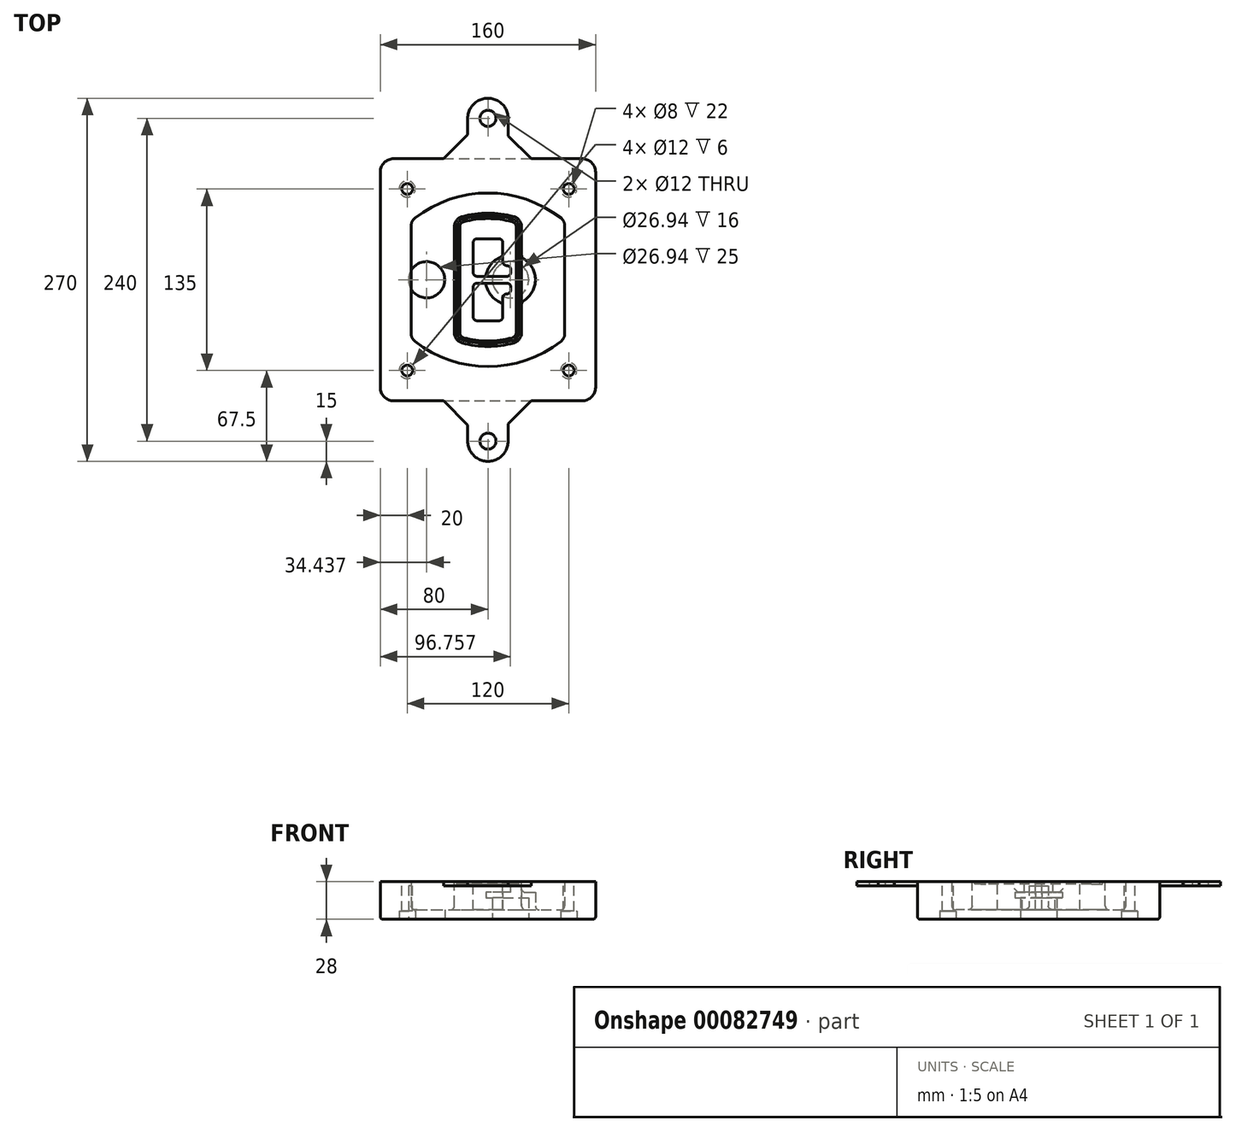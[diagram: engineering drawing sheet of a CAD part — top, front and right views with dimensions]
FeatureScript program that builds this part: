
annotation { "Feature Type Name" : "Feature", "Feature Type Description" : "" }
export const myFeature = defineFeature(function(context is Context, id is Id, definition is map)
    precondition{}
    {
        {
            var Q0;
            Q0=qCreatedBy(makeId("Top.planeOp"),FACE);
            var sketch = newSketch(context, id + "F0", { "sketchPlane" : qUnion([Q0])});
            skPoint(sketch, "E0.rect.middle", {"position": v(0, 0) * mm});
            skLineSegment(sketch, "E1.bottom", {"start": v(-70, -90) * mm, "end": v(70, -90) * mm});
            skLineSegment(sketch, "E1.top", {"start": v(-70, 90) * mm, "end": v(70, 90) * mm});
            skLineSegment(sketch, "E1.left", {"start": v(-80, -80) * mm, "end": v(-80, 80) * mm});
            skLineSegment(sketch, "E1.right", {"start": v(80, -80) * mm, "end": v(80, 80) * mm});
            skLineSegment(sketch, "E2", {"start": v(-80, 90) * mm, "end": v(80, -90) * mm, "construction": true});
            skLineSegment(sketch, "E3", {"start": v(80, 90) * mm, "end": v(-80, -90) * mm, "construction": true});
            skCircle(sketch, "E4", {"center": v(-60, 67.5) * mm, "radius": 4 * mm});
            skCircle(sketch, "E5", {"center": v(60, 67.5) * mm, "radius": 4 * mm});
            skCircle(sketch, "E6", {"center": v(60, -67.5) * mm, "radius": 4 * mm});
            skCircle(sketch, "E7", {"center": v(-60, -67.5) * mm, "radius": 4 * mm});
            skLineSegment(sketch, "E8", {"start": v(-60, 67.5) * mm, "end": v(60, 67.5) * mm, "construction": true});
            skLineSegment(sketch, "E9", {"start": v(60, 67.5) * mm, "end": v(60, -67.5) * mm, "construction": true});
            skLineSegment(sketch, "E10", {"start": v(60, -67.5) * mm, "end": v(-60, -67.5) * mm, "construction": true});
            skLineSegment(sketch, "E11", {"start": v(-60, -67.5) * mm, "end": v(-60, 67.5) * mm, "construction": true});
            skLineSegment(sketch, "E12", {"start": v(-60, 40.3) * mm, "end": v(-60, -40.3) * mm});
            skLineSegment(sketch, "E13", {"start": v(60, 40.3) * mm, "end": v(60, -40.3) * mm});
            skArc(sketch, "E14", {"start": v(56.15, 48.18) * mm, "mid": v(0, 67.5) * mm, "end": v(-56.15, 48.18) * mm});
            skArc(sketch, "E15", {"start": v(-56.15, -48.18) * mm, "mid": v(0, -67.5) * mm, "end": v(56.15, -48.18) * mm});
            skLineSegment(sketch, "E16", {"start": v(-60, 0) * mm, "end": v(60, 0) * mm, "construction": true});
            skPoint(sketch, "E17.visualSharp", {"position": v(-60, -45) * mm});
            skArc(sketch, "E17.filletArc", {"start": v(-60, -40.3) * mm, "mid": v(-58.99, -44.68) * mm, "end": v(-56.15, -48.18) * mm});
            skPoint(sketch, "E18.visualSharp", {"position": v(-60, 45) * mm});
            skArc(sketch, "E18.filletArc", {"start": v(-56.15, 48.18) * mm, "mid": v(-58.99, 44.68) * mm, "end": v(-60, 40.3) * mm});
            skPoint(sketch, "E19.visualSharp", {"position": v(60, 45) * mm});
            skArc(sketch, "E19.filletArc", {"start": v(60, 40.3) * mm, "mid": v(58.99, 44.68) * mm, "end": v(56.15, 48.18) * mm});
            skPoint(sketch, "E20.visualSharp", {"position": v(60, -45) * mm});
            skArc(sketch, "E20.filletArc", {"start": v(56.15, -48.18) * mm, "mid": v(58.99, -44.68) * mm, "end": v(60, -40.3) * mm});
            skPoint(sketch, "E21.visualSharp", {"position": v(-80, 90) * mm});
            skArc(sketch, "E21.filletArc", {"start": v(-70, 90) * mm, "mid": v(-77.07, 87.07) * mm, "end": v(-80, 80) * mm});
            skPoint(sketch, "E22.visualSharp", {"position": v(80, 90) * mm});
            skArc(sketch, "E22.filletArc", {"start": v(80, 80) * mm, "mid": v(77.07, 87.07) * mm, "end": v(70, 90) * mm});
            skPoint(sketch, "E23.visualSharp", {"position": v(80, -90) * mm});
            skArc(sketch, "E23.filletArc", {"start": v(70, -90) * mm, "mid": v(77.07, -87.07) * mm, "end": v(80, -80) * mm});
            skPoint(sketch, "E24.visualSharp", {"position": v(-80, -90) * mm});
            skArc(sketch, "E24.filletArc", {"start": v(-80, -80) * mm, "mid": v(-77.07, -87.07) * mm, "end": v(-70, -90) * mm});
            skArc(sketch, "E25.0", {"start": v(57, 40.3) * mm, "mid": v(56.3, 43.36) * mm, "end": v(54.3, 45.81) * mm});
            skLineSegment(sketch, "E25.1", {"start": v(57, 40.3) * mm, "end": v(57, -40.3) * mm});
            skArc(sketch, "E25.2", {"start": v(54.3, -45.81) * mm, "mid": v(56.3, -43.36) * mm, "end": v(57, -40.3) * mm});
            skArc(sketch, "E25.3", {"start": v(-54.3, -45.81) * mm, "mid": v(0, -64.5) * mm, "end": v(54.3, -45.81) * mm});
            skArc(sketch, "E25.4", {"start": v(-57, -40.3) * mm, "mid": v(-56.3, -43.36) * mm, "end": v(-54.3, -45.81) * mm});
            skArc(sketch, "E25.5", {"start": v(54.3, 45.81) * mm, "mid": v(0, 64.5) * mm, "end": v(-54.3, 45.81) * mm});
            skLineSegment(sketch, "E25.6", {"start": v(-57, 40.3) * mm, "end": v(-57, -40.3) * mm});
            skArc(sketch, "E25.7", {"start": v(-54.3, 45.81) * mm, "mid": v(-56.3, 43.36) * mm, "end": v(-57, 40.3) * mm});
            skArc(sketch, "E26.0", {"start": v(-58.62, 51.33) * mm, "mid": v(-62.58, 46.43) * mm, "end": v(-64, 40.3) * mm});
            skArc(sketch, "E26.1", {"start": v(58.62, 51.33) * mm, "mid": v(0, 71.5) * mm, "end": v(-58.62, 51.33) * mm});
            skArc(sketch, "E26.2", {"start": v(64, 40.3) * mm, "mid": v(62.58, 46.43) * mm, "end": v(58.62, 51.33) * mm});
            skLineSegment(sketch, "E26.3", {"start": v(64, 40.3) * mm, "end": v(64, -40.3) * mm});
            skArc(sketch, "E26.4", {"start": v(58.62, -51.33) * mm, "mid": v(62.58, -46.43) * mm, "end": v(64, -40.3) * mm});
            skLineSegment(sketch, "E26.5", {"start": v(-64, 40.3) * mm, "end": v(-64, -40.3) * mm});
            skArc(sketch, "E26.6", {"start": v(-58.62, -51.33) * mm, "mid": v(0, -71.5) * mm, "end": v(58.62, -51.33) * mm});
            skArc(sketch, "E26.7", {"start": v(-64, -40.3) * mm, "mid": v(-62.58, -46.43) * mm, "end": v(-58.62, -51.33) * mm});
            skSolve(sketch);
        }
        {
            var Q0;
            Q0=makeQuery(id+"F0.imprint","IMPRINT",FACE,{"disambiguationData":[TD([[makeQuery(id+"F0.imprint","IMPRINT",EDGE,{"derivedFrom":sQuery(id+"F0.wireOp",EDGE,"E1.bottom")}),1.0]])]});
            var Q1;
            Q1=makeQuery(id+"F0.imprint","IMPRINT",FACE,{"disambiguationData":[TD([[makeQuery(id+"F0.imprint","IMPRINT",EDGE,{"derivedFrom":sQuery(id+"F0.wireOp",EDGE,"E12")}),1.0]])]});
            var Q2;
            Q2=makeQuery(id+"F0.imprint","IMPRINT",FACE,{"disambiguationData":[TD([[makeQuery(id+"F0.imprint","IMPRINT",EDGE,{"derivedFrom":sQuery(id+"F0.wireOp",EDGE,"E25.0")}),1.0]])]});
            var Q3;
            Q3=makeQuery(id+"F0.imprint","IMPRINT",FACE,{"disambiguationData":[TD([[makeQuery(id+"F0.imprint","IMPRINT",EDGE,{"derivedFrom":sQuery(id+"F0.wireOp",EDGE,"E12")}),-1.0]])]});
            extrude(context, id + "F1", {"entities" : qUnion([Q0, Q1, Q2, Q3]), "oppositeDirection" : true, "depth" : 25 * mm});
        }
        {
            var Q0;
            Q0=makeQuery(id+"F0.imprint","IMPRINT",FACE,{"disambiguationData":[TD([[makeQuery(id+"F0.imprint","IMPRINT",EDGE,{"derivedFrom":sQuery(id+"F0.wireOp",EDGE,"E12")}),1.0]])]});
            extrude(context, id + "F2", {"entities" : qUnion([Q0]), "operationType" : NewBodyOperationType.ADD, "depth" : 3 * mm});
        }
        {
            var Q0;
            Q0=makeQuery(id+"F0.imprint","IMPRINT",FACE,{"disambiguationData":[TD([[makeQuery(id+"F0.imprint","IMPRINT",EDGE,{"derivedFrom":sQuery(id+"F0.wireOp",EDGE,"E25.0")}),1.0]])]});
            extrude(context, id + "F3", {"entities" : qUnion([Q0]), "operationType" : NewBodyOperationType.REMOVE, "oppositeDirection" : true, "depth" : 18 * mm});
        }
        {
            var Q0;
            Q0=makeQuery(id+"F2.opExtrude","CAP_FACE",FACE,{"disambiguationData":[OSD([sQuery(id+"F0.wireOp",EDGE,"E12"),sQuery(id+"F0.wireOp",EDGE,"E13"),sQuery(id+"F0.wireOp",EDGE,"E14"),sQuery(id+"F0.wireOp",EDGE,"E15"),sQuery(id+"F0.wireOp",EDGE,"E17.filletArc"),sQuery(id+"F0.wireOp",EDGE,"E18.filletArc"),sQuery(id+"F0.wireOp",EDGE,"E19.filletArc"),sQuery(id+"F0.wireOp",EDGE,"E20.filletArc"),sQuery(id+"F0.wireOp",EDGE,"E25.0"),sQuery(id+"F0.wireOp",EDGE,"E25.1"),sQuery(id+"F0.wireOp",EDGE,"E25.2"),sQuery(id+"F0.wireOp",EDGE,"E25.3"),sQuery(id+"F0.wireOp",EDGE,"E25.4"),sQuery(id+"F0.wireOp",EDGE,"E25.5"),sQuery(id+"F0.wireOp",EDGE,"E25.6"),sQuery(id+"F0.wireOp",EDGE,"E25.7")])],"isStart":false});
            var sketch = newSketch(context, id + "F4", { "sketchPlane" : qUnion([Q0])});
            skArc(sketch, "E27.0", {"start": v(-19.08, -46.97) * mm, "mid": v(0, -49.5) * mm, "end": v(19.08, -46.97) * mm});
            skArc(sketch, "E28.0", {"start": v(19.08, 46.97) * mm, "mid": v(0, 49.5) * mm, "end": v(-19.08, 46.97) * mm});
            skLineSegment(sketch, "E29", {"start": v(-25, 39.25) * mm, "end": v(-25, -39.25) * mm});
            skLineSegment(sketch, "E30", {"start": v(25, 39.25) * mm, "end": v(25, -39.25) * mm});
            skLineSegment(sketch, "E31", {"start": v(-25, 45.1) * mm, "end": v(25, 45.1) * mm, "construction": true});
            skLineSegment(sketch, "E32", {"start": v(-25, -45.1) * mm, "end": v(25, -45.1) * mm, "construction": true});
            skPoint(sketch, "E33.visualSharp", {"position": v(-25, 45.1) * mm});
            skArc(sketch, "E33.filletArc", {"start": v(-19.08, 46.97) * mm, "mid": v(-23.35, 44.11) * mm, "end": v(-25, 39.25) * mm});
            skPoint(sketch, "E34.visualSharp", {"position": v(25, 45.1) * mm});
            skArc(sketch, "E34.filletArc", {"start": v(25, 39.25) * mm, "mid": v(23.35, 44.11) * mm, "end": v(19.08, 46.97) * mm});
            skPoint(sketch, "E35.visualSharp", {"position": v(25, -45.1) * mm});
            skArc(sketch, "E35.filletArc", {"start": v(19.08, -46.97) * mm, "mid": v(23.35, -44.11) * mm, "end": v(25, -39.25) * mm});
            skPoint(sketch, "E36.visualSharp", {"position": v(-25, -45.1) * mm});
            skArc(sketch, "E36.filletArc", {"start": v(-25, -39.25) * mm, "mid": v(-23.35, -44.11) * mm, "end": v(-19.08, -46.97) * mm});
            skArc(sketch, "E37.0", {"start": v(54.3, 45.81) * mm, "mid": v(0, 64.5) * mm, "end": v(-54.3, 45.81) * mm});
            skArc(sketch, "E37.1", {"start": v(-54.3, 45.81) * mm, "mid": v(-56.3, 43.36) * mm, "end": v(-57, 40.3) * mm});
            skLineSegment(sketch, "E37.2", {"start": v(-57, 40.3) * mm, "end": v(-57, -40.3) * mm});
            skArc(sketch, "E37.3", {"start": v(-57, -40.3) * mm, "mid": v(-56.3, -43.36) * mm, "end": v(-54.3, -45.81) * mm});
            skArc(sketch, "E37.4", {"start": v(-54.3, -45.81) * mm, "mid": v(0, -64.5) * mm, "end": v(54.3, -45.81) * mm});
            skArc(sketch, "E37.5", {"start": v(54.3, -45.81) * mm, "mid": v(56.3, -43.36) * mm, "end": v(57, -40.3) * mm});
            skLineSegment(sketch, "E37.6", {"start": v(57, 40.3) * mm, "end": v(57, -40.3) * mm});
            skArc(sketch, "E37.7", {"start": v(57, 40.3) * mm, "mid": v(56.3, 43.36) * mm, "end": v(54.3, 45.81) * mm});
            skLineSegment(sketch, "E38.0", {"start": v(23, 39.25) * mm, "end": v(23, -39.25) * mm});
            skArc(sketch, "E38.1", {"start": v(18.56, -45.04) * mm, "mid": v(21.76, -42.9) * mm, "end": v(23, -39.25) * mm});
            skArc(sketch, "E38.2", {"start": v(-18.56, -45.04) * mm, "mid": v(0, -47.5) * mm, "end": v(18.56, -45.04) * mm});
            skArc(sketch, "E38.3", {"start": v(-23, -39.25) * mm, "mid": v(-21.76, -42.9) * mm, "end": v(-18.56, -45.04) * mm});
            skLineSegment(sketch, "E38.4", {"start": v(-23, 39.25) * mm, "end": v(-23, -39.25) * mm});
            skArc(sketch, "E38.5", {"start": v(23, 39.25) * mm, "mid": v(21.76, 42.9) * mm, "end": v(18.56, 45.04) * mm});
            skArc(sketch, "E38.6", {"start": v(-18.56, 45.04) * mm, "mid": v(-21.76, 42.9) * mm, "end": v(-23, 39.25) * mm});
            skArc(sketch, "E38.7", {"start": v(18.56, 45.04) * mm, "mid": v(0, 47.5) * mm, "end": v(-18.56, 45.04) * mm});
            skArc(sketch, "E39.0", {"start": v(21, 39.25) * mm, "mid": v(20.18, 41.68) * mm, "end": v(18.04, 43.1) * mm});
            skLineSegment(sketch, "E39.1", {"start": v(21, 39.25) * mm, "end": v(21, -39.25) * mm});
            skArc(sketch, "E39.2", {"start": v(18.04, -43.1) * mm, "mid": v(20.18, -41.68) * mm, "end": v(21, -39.25) * mm});
            skArc(sketch, "E39.3", {"start": v(-18.04, -43.1) * mm, "mid": v(0, -45.5) * mm, "end": v(18.04, -43.1) * mm});
            skArc(sketch, "E39.4", {"start": v(-21, -39.25) * mm, "mid": v(-20.18, -41.68) * mm, "end": v(-18.04, -43.1) * mm});
            skArc(sketch, "E39.5", {"start": v(18.04, 43.1) * mm, "mid": v(0, 45.5) * mm, "end": v(-18.04, 43.1) * mm});
            skLineSegment(sketch, "E39.6", {"start": v(-21, 39.25) * mm, "end": v(-21, -39.25) * mm});
            skArc(sketch, "E39.7", {"start": v(-18.04, 43.1) * mm, "mid": v(-20.18, 41.68) * mm, "end": v(-21, 39.25) * mm});
            skLineSegment(sketch, "E40", {"start": v(-25, 0) * mm, "end": v(25, 0) * mm, "construction": true});
            skLineSegment(sketch, "E41", {"start": v(-11, 5.5) * mm, "end": v(-11, 27.5) * mm});
            skLineSegment(sketch, "E42", {"start": v(-8, 30.5) * mm, "end": v(8, 30.5) * mm});
            skLineSegment(sketch, "E43", {"start": v(11, 27.5) * mm, "end": v(11, 13.5) * mm});
            skLineSegment(sketch, "E44", {"start": v(14, 10.5) * mm, "end": v(14, 10.5) * mm});
            skLineSegment(sketch, "E45", {"start": v(17, 7.5) * mm, "end": v(17, 5.5) * mm});
            skLineSegment(sketch, "E46", {"start": v(14, 2.5) * mm, "end": v(-8, 2.5) * mm});
            skPoint(sketch, "E47.visualSharp", {"position": v(-11, 30.5) * mm});
            skArc(sketch, "E47.filletArc", {"start": v(-8, 30.5) * mm, "mid": v(-10.12, 29.62) * mm, "end": v(-11, 27.5) * mm});
            skPoint(sketch, "E48.visualSharp", {"position": v(11, 30.5) * mm});
            skArc(sketch, "E48.filletArc", {"start": v(11, 27.5) * mm, "mid": v(10.12, 29.62) * mm, "end": v(8, 30.5) * mm});
            skPoint(sketch, "E49.visualSharp", {"position": v(11, 10.5) * mm});
            skArc(sketch, "E49.filletArc", {"start": v(11, 13.5) * mm, "mid": v(11.88, 11.38) * mm, "end": v(14, 10.5) * mm});
            skPoint(sketch, "E50.visualSharp", {"position": v(17, 10.5) * mm});
            skArc(sketch, "E50.filletArc", {"start": v(17, 7.5) * mm, "mid": v(16.12, 9.62) * mm, "end": v(14, 10.5) * mm});
            skPoint(sketch, "E51.visualSharp", {"position": v(17, 2.5) * mm});
            skArc(sketch, "E51.filletArc", {"start": v(14, 2.5) * mm, "mid": v(16.12, 3.38) * mm, "end": v(17, 5.5) * mm});
            skPoint(sketch, "E52.visualSharp", {"position": v(-11, 2.5) * mm});
            skArc(sketch, "E52.filletArc", {"start": v(-11, 5.5) * mm, "mid": v(-10.12, 3.38) * mm, "end": v(-8, 2.5) * mm});
            skLineSegment(sketch, "E53.0.MirrorCS", {"start": v(14, -2.5) * mm, "end": v(-8, -2.5) * mm});
            skArc(sketch, "E54.0.MirrorCS", {"start": v(-11, -5.5) * mm, "mid": v(-10.12, -3.38) * mm, "end": v(-8, -2.5) * mm});
            skLineSegment(sketch, "E55.0.MirrorCS", {"start": v(-11, -5.5) * mm, "end": v(-11, -27.5) * mm});
            skArc(sketch, "E56.0.MirrorCS", {"start": v(-8, -30.5) * mm, "mid": v(-10.12, -29.62) * mm, "end": v(-11, -27.5) * mm});
            skLineSegment(sketch, "E57.0.MirrorCS", {"start": v(-8, -30.5) * mm, "end": v(8, -30.5) * mm});
            skArc(sketch, "E58.0.MirrorCS", {"start": v(11, -27.5) * mm, "mid": v(10.12, -29.62) * mm, "end": v(8, -30.5) * mm});
            skLineSegment(sketch, "E59.0.MirrorCS", {"start": v(11, -27.5) * mm, "end": v(11, -13.5) * mm});
            skArc(sketch, "E60.0.MirrorCS", {"start": v(11, -13.5) * mm, "mid": v(11.88, -11.38) * mm, "end": v(14, -10.5) * mm});
            skArc(sketch, "E61.0.MirrorCS", {"start": v(17, -7.5) * mm, "mid": v(16.12, -9.62) * mm, "end": v(14, -10.5) * mm});
            skLineSegment(sketch, "E62.0.MirrorCS", {"start": v(17, -7.5) * mm, "end": v(17, -5.5) * mm});
            skArc(sketch, "E63.0.MirrorCS", {"start": v(14, -2.5) * mm, "mid": v(16.12, -3.38) * mm, "end": v(17, -5.5) * mm});
            skSolve(sketch);
        }
        {
            var Q0;
            Q0=makeQuery(id+"F4.imprint","IMPRINT",FACE,{"disambiguationData":[TD([[makeQuery(id+"F4.imprint","IMPRINT",EDGE,{"derivedFrom":sQuery(id+"F4.wireOp",EDGE,"E27.0")}),1.0]])]});
            var Q1;
            Q1=makeQuery(id+"F4.imprint","IMPRINT",FACE,{"disambiguationData":[TD([[makeQuery(id+"F4.imprint","IMPRINT",EDGE,{"derivedFrom":sQuery(id+"F4.wireOp",EDGE,"E38.0")}),-1.0]])]});
            var Q2;
            Q2=makeQuery(id+"F4.imprint","IMPRINT",FACE,{"disambiguationData":[TD([[makeQuery(id+"F4.imprint","IMPRINT",EDGE,{"derivedFrom":sQuery(id+"F4.wireOp",EDGE,"E39.0")}),1.0]])]});
            extrude(context, id + "F5", {"entities" : qUnion([Q0, Q1, Q2]), "operationType" : NewBodyOperationType.ADD, "endBound" : BoundingType.UP_TO_NEXT, "oppositeDirection" : true, "depth" : 25 * mm});
        }
        {
            var Q0;
            Q0=makeQuery(id+"F4.imprint","IMPRINT",FACE,{"disambiguationData":[TD([[makeQuery(id+"F4.imprint","IMPRINT",EDGE,{"derivedFrom":sQuery(id+"F4.wireOp",EDGE,"E38.0")}),-1.0]])]});
            extrude(context, id + "F6", {"entities" : qUnion([Q0]), "operationType" : NewBodyOperationType.REMOVE, "oppositeDirection" : true, "depth" : 2 * mm});
        }
        {
            var Q0;
            Q0=makeQuery(id+"F1.opExtrude","CAP_FACE",FACE,{"disambiguationData":[OSD([sQuery(id+"F0.wireOp",EDGE,"E1.bottom"),sQuery(id+"F0.wireOp",EDGE,"E1.top"),sQuery(id+"F0.wireOp",EDGE,"E1.left"),sQuery(id+"F0.wireOp",EDGE,"E1.right"),sQuery(id+"F0.wireOp",EDGE,"E4"),sQuery(id+"F0.wireOp",EDGE,"E5"),sQuery(id+"F0.wireOp",EDGE,"E6"),sQuery(id+"F0.wireOp",EDGE,"E7"),sQuery(id+"F0.wireOp",EDGE,"E21.filletArc"),sQuery(id+"F0.wireOp",EDGE,"E22.filletArc"),sQuery(id+"F0.wireOp",EDGE,"E23.filletArc"),sQuery(id+"F0.wireOp",EDGE,"E24.filletArc")])],"isStart":false});
            var sketch = newSketch(context, id + "F7", { "sketchPlane" : qUnion([Q0])});
            skCircle(sketch, "E64", {"center": v(16.76, 0) * mm, "radius": 13.47 * mm});
            skCircle(sketch, "E65", {"center": v(-45.56, 0) * mm, "radius": 13.47 * mm});
            skLineSegment(sketch, "E66", {"start": v(80, 0) * mm, "end": v(-80, 0) * mm});
            skCircle(sketch, "E67", {"center": v(16.76, 0) * mm, "radius": 18.47 * mm});
            skCircle(sketch, "E68", {"center": v(60, -67.5) * mm, "radius": 6 * mm});
            skCircle(sketch, "E69", {"center": v(-60, -67.5) * mm, "radius": 6 * mm});
            skCircle(sketch, "E70", {"center": v(-60, 67.5) * mm, "radius": 6 * mm});
            skCircle(sketch, "E71", {"center": v(60, 67.5) * mm, "radius": 6 * mm});
            skSolve(sketch);
        }
        {
            var Q0;
            {var subQ1=sQuery(id+"F7.wireOp",EDGE,"E66");var subQ4=sQuery(id+"F7.wireOp",EDGE,"E64");var subQ6=makeQuery(id+"F7.imprint","INTERSECT",VERTEX,{"disambiguationData":[OD(0.0)],"derivedFrom":[subQ4,subQ1]});Q0=makeQuery(id+"F7.imprint","IMPRINT",FACE,{"disambiguationData":[TD([[makeQuery(id+"F7.imprint","IMPRINT",EDGE,{"disambiguationData":[TD([[subQ6,-1.0]])],"derivedFrom":subQ4}),-1.0]])]});}
            var Q1;
            {var subQ0=sQuery(id+"F7.wireOp",EDGE,"E66");var subQ1=sQuery(id+"F7.wireOp",EDGE,"E64");var subQ3=makeQuery(id+"F7.imprint","INTERSECT",VERTEX,{"disambiguationData":[OD(0.0)],"derivedFrom":[subQ1,subQ0]});Q1=makeQuery(id+"F7.imprint","IMPRINT",FACE,{"disambiguationData":[TD([[makeQuery(id+"F7.imprint","IMPRINT",EDGE,{"disambiguationData":[TD([[subQ3,-1.0]])],"derivedFrom":subQ1}),1.0]])]});}
            var Q2;
            {var subQ0=sQuery(id+"F7.wireOp",EDGE,"E66");var subQ1=sQuery(id+"F7.wireOp",EDGE,"E64");var subQ3=makeQuery(id+"F7.imprint","INTERSECT",VERTEX,{"disambiguationData":[OD(0.0)],"derivedFrom":[subQ1,subQ0]});Q2=makeQuery(id+"F7.imprint","IMPRINT",FACE,{"disambiguationData":[TD([[makeQuery(id+"F7.imprint","IMPRINT",EDGE,{"disambiguationData":[TD([[subQ3,1.0]])],"derivedFrom":subQ1}),1.0]])]});}
            var Q3;
            {var subQ1=sQuery(id+"F7.wireOp",EDGE,"E66");var subQ4=sQuery(id+"F7.wireOp",EDGE,"E64");var subQ6=makeQuery(id+"F7.imprint","INTERSECT",VERTEX,{"disambiguationData":[OD(0.0)],"derivedFrom":[subQ4,subQ1]});Q3=makeQuery(id+"F7.imprint","IMPRINT",FACE,{"disambiguationData":[TD([[makeQuery(id+"F7.imprint","IMPRINT",EDGE,{"disambiguationData":[TD([[subQ6,1.0]])],"derivedFrom":subQ4}),-1.0]])]});}
            extrude(context, id + "F8", {"entities" : qUnion([Q0, Q1, Q2, Q3]), "operationType" : NewBodyOperationType.ADD, "oppositeDirection" : true, "depth" : 20 * mm});
        }
        {
            var Q0;
            {var subQ0=sQuery(id+"F7.wireOp",EDGE,"E66");var subQ1=sQuery(id+"F7.wireOp",EDGE,"E64");var subQ3=makeQuery(id+"F7.imprint","INTERSECT",VERTEX,{"disambiguationData":[OD(0.0)],"derivedFrom":[subQ1,subQ0]});Q0=makeQuery(id+"F7.imprint","IMPRINT",FACE,{"disambiguationData":[TD([[makeQuery(id+"F7.imprint","IMPRINT",EDGE,{"disambiguationData":[TD([[subQ3,-1.0]])],"derivedFrom":subQ1}),1.0]])]});}
            var Q1;
            {var subQ0=sQuery(id+"F7.wireOp",EDGE,"E66");var subQ1=sQuery(id+"F7.wireOp",EDGE,"E64");var subQ3=makeQuery(id+"F7.imprint","INTERSECT",VERTEX,{"disambiguationData":[OD(0.0)],"derivedFrom":[subQ1,subQ0]});Q1=makeQuery(id+"F7.imprint","IMPRINT",FACE,{"disambiguationData":[TD([[makeQuery(id+"F7.imprint","IMPRINT",EDGE,{"disambiguationData":[TD([[subQ3,1.0]])],"derivedFrom":subQ1}),1.0]])]});}
            extrude(context, id + "F9", {"entities" : qUnion([Q0, Q1]), "operationType" : NewBodyOperationType.REMOVE, "oppositeDirection" : true, "depth" : 16 * mm});
        }
        {
            var Q0;
            {var subQ0=sQuery(id+"F7.wireOp",EDGE,"E66");var subQ1=sQuery(id+"F7.wireOp",EDGE,"E65");var subQ3=makeQuery(id+"F7.imprint","INTERSECT",VERTEX,{"disambiguationData":[OD(0.0)],"derivedFrom":[subQ1,subQ0]});Q0=makeQuery(id+"F7.imprint","IMPRINT",FACE,{"disambiguationData":[TD([[makeQuery(id+"F7.imprint","IMPRINT",EDGE,{"disambiguationData":[TD([[subQ3,-1.0]])],"derivedFrom":subQ1}),1.0]])]});}
            var Q1;
            {var subQ0=sQuery(id+"F7.wireOp",EDGE,"E66");var subQ1=sQuery(id+"F7.wireOp",EDGE,"E65");var subQ3=makeQuery(id+"F7.imprint","INTERSECT",VERTEX,{"disambiguationData":[OD(0.0)],"derivedFrom":[subQ1,subQ0]});Q1=makeQuery(id+"F7.imprint","IMPRINT",FACE,{"disambiguationData":[TD([[makeQuery(id+"F7.imprint","IMPRINT",EDGE,{"disambiguationData":[TD([[subQ3,1.0]])],"derivedFrom":subQ1}),1.0]])]});}
            extrude(context, id + "F10", {"entities" : qUnion([Q0, Q1]), "operationType" : NewBodyOperationType.REMOVE, "oppositeDirection" : true, "depth" : 25 * mm});
        }
        {
            var Q0;
            Q0=makeQuery(id+"F7.imprint","IMPRINT",FACE,{"disambiguationData":[TD([[makeQuery(id+"F7.imprint","IMPRINT",EDGE,{"derivedFrom":sQuery(id+"F7.wireOp",EDGE,"E68")}),1.0]])]});
            var Q1;
            Q1=makeQuery(id+"F7.imprint","IMPRINT",FACE,{"disambiguationData":[TD([[makeQuery(id+"F7.imprint","IMPRINT",EDGE,{"derivedFrom":makeQuery(id+"F1.opExtrude","CAP_EDGE",EDGE,{"disambiguationData":[OSD([sQuery(id+"F0.wireOp",EDGE,"E5")])],"isStart":false})}),-1.0]])]});
            var Q2;
            Q2=makeQuery(id+"F7.imprint","IMPRINT",FACE,{"disambiguationData":[TD([[makeQuery(id+"F7.imprint","IMPRINT",EDGE,{"derivedFrom":sQuery(id+"F7.wireOp",EDGE,"E69")}),1.0]])]});
            var Q3;
            Q3=makeQuery(id+"F7.imprint","IMPRINT",FACE,{"disambiguationData":[TD([[makeQuery(id+"F7.imprint","IMPRINT",EDGE,{"derivedFrom":makeQuery(id+"F1.opExtrude","CAP_EDGE",EDGE,{"disambiguationData":[OSD([sQuery(id+"F0.wireOp",EDGE,"E4")])],"isStart":false})}),-1.0]])]});
            var Q4;
            Q4=makeQuery(id+"F7.imprint","IMPRINT",FACE,{"disambiguationData":[TD([[makeQuery(id+"F7.imprint","IMPRINT",EDGE,{"derivedFrom":sQuery(id+"F7.wireOp",EDGE,"E70")}),1.0]])]});
            var Q5;
            Q5=makeQuery(id+"F7.imprint","IMPRINT",FACE,{"disambiguationData":[TD([[makeQuery(id+"F7.imprint","IMPRINT",EDGE,{"derivedFrom":makeQuery(id+"F1.opExtrude","CAP_EDGE",EDGE,{"disambiguationData":[OSD([sQuery(id+"F0.wireOp",EDGE,"E7")])],"isStart":false})}),-1.0]])]});
            var Q6;
            Q6=makeQuery(id+"F7.imprint","IMPRINT",FACE,{"disambiguationData":[TD([[makeQuery(id+"F7.imprint","IMPRINT",EDGE,{"derivedFrom":sQuery(id+"F7.wireOp",EDGE,"E71")}),1.0]])]});
            var Q7;
            Q7=makeQuery(id+"F7.imprint","IMPRINT",FACE,{"disambiguationData":[TD([[makeQuery(id+"F7.imprint","IMPRINT",EDGE,{"derivedFrom":makeQuery(id+"F1.opExtrude","CAP_EDGE",EDGE,{"disambiguationData":[OSD([sQuery(id+"F0.wireOp",EDGE,"E6")])],"isStart":false})}),-1.0]])]});
            extrude(context, id + "F11", {"entities" : qUnion([Q0, Q1, Q2, Q3, Q4, Q5, Q6, Q7]), "operationType" : NewBodyOperationType.REMOVE, "oppositeDirection" : true, "depth" : 6 * mm});
        }
        {
            var Q0;
            Q0=makeQuery(id+"F9.boolean.opBoolean","COPY",FACE,{"derivedFrom":makeQuery(id+"F9.opExtrude","CAP_FACE",FACE,{"disambiguationData":[OSD([sQuery(id+"F7.wireOp",EDGE,"E64")])],"isStart":false})});
            var sketch = newSketch(context, id + "F12", { "sketchPlane" : qUnion([Q0])});
            skArc(sketch, "E72.0", {"start": v(11, 17.55) * mm, "mid": v(2.57, 11.82) * mm, "end": v(-1.54, 2.5) * mm});
            skArc(sketch, "E72.1", {"start": v(-1.54, -2.5) * mm, "mid": v(2.57, -11.82) * mm, "end": v(11, -17.55) * mm});
            skLineSegment(sketch, "E73", {"start": v(-1.54, -2.5) * mm, "end": v(14, -2.5) * mm});
            skLineSegment(sketch, "E74.0", {"start": v(14, 2.5) * mm, "end": v(-1.54, 2.5) * mm});
            skArc(sketch, "E74.1", {"start": v(14, 2.5) * mm, "mid": v(16.12, 3.38) * mm, "end": v(17, 5.5) * mm});
            skLineSegment(sketch, "E74.2", {"start": v(17, 7.5) * mm, "end": v(17, 5.5) * mm});
            skArc(sketch, "E74.3", {"start": v(17, 7.5) * mm, "mid": v(16.12, 9.62) * mm, "end": v(14, 10.5) * mm});
            skArc(sketch, "E74.4", {"start": v(11, 13.5) * mm, "mid": v(11.88, 11.38) * mm, "end": v(14, 10.5) * mm});
            skLineSegment(sketch, "E74.5", {"start": v(11, 17.55) * mm, "end": v(11, 13.5) * mm});
            skLineSegment(sketch, "E74.7", {"start": v(14, -2.5) * mm, "end": v(-1.54, -2.5) * mm});
            skArc(sketch, "E74.8", {"start": v(14, -2.5) * mm, "mid": v(16.12, -3.38) * mm, "end": v(17, -5.5) * mm});
            skLineSegment(sketch, "E74.9", {"start": v(17, -7.5) * mm, "end": v(17, -5.5) * mm});
            skArc(sketch, "E74.10", {"start": v(17, -7.5) * mm, "mid": v(16.12, -9.62) * mm, "end": v(14, -10.5) * mm});
            skArc(sketch, "E74.11", {"start": v(11, -13.5) * mm, "mid": v(11.88, -11.38) * mm, "end": v(14, -10.5) * mm});
            skLineSegment(sketch, "E74.12", {"start": v(11, -17.55) * mm, "end": v(11, -13.5) * mm});
            skPoint(sketch, "E75.orphan", {"position": v(11, -27.5) * mm});
            skPoint(sketch, "E76.orphan", {"position": v(-8, -2.5) * mm});
            skPoint(sketch, "E77.orphan", {"position": v(-8, 2.5) * mm});
            skPoint(sketch, "E78.orphan", {"position": v(11, 27.5) * mm});
            skSolve(sketch);
        }
        {
            var Q0;
            {var subQ7=sQuery(id+"F12.wireOp",EDGE,"E72.0");var subQ14=sQuery(id+"F12.wireOp",EDGE,"E72.1");var subQ16=sQuery(id+"F12.wireOp",EDGE,"E74.1");var subQ18=sQuery(id+"F12.wireOp",EDGE,"E74.8");Q0=qUnion([makeQuery(id+"F12.imprint","IMPRINT",FACE,{"disambiguationData":[TD([[makeQuery(id+"F12.imprint","IMPRINT",EDGE,{"derivedFrom":subQ7}),1.0]])]}),makeQuery(id+"F12.imprint","IMPRINT",FACE,{"disambiguationData":[TD([[makeQuery(id+"F12.imprint","IMPRINT",EDGE,{"derivedFrom":subQ14}),1.0]])]}),makeQuery(id+"F12.imprint","IMPRINT",FACE,{"disambiguationData":[TD([[makeQuery(id+"F12.imprint","IMPRINT",EDGE,{"derivedFrom":subQ16}),1.0]])]}),makeQuery(id+"F12.imprint","IMPRINT",FACE,{"disambiguationData":[TD([[makeQuery(id+"F12.imprint","IMPRINT",EDGE,{"derivedFrom":subQ18}),-1.0]])]})]);}
            var Q1;
            Q1=makeQuery(id+"F5.boolean.opBoolean","SPLIT",FACE,{"disambiguationData":[TD([makeQuery(id+"F5.opExtrude","SWEPT_FACE",FACE,{"disambiguationData":[OSD([sQuery(id+"F4.wireOp",EDGE,"E41")])]})])],"derivedFrom":makeQuery(id+"F3.boolean.opBoolean","COPY",FACE,{"derivedFrom":makeQuery(id+"F3.opExtrude","CAP_FACE",FACE,{"disambiguationData":[OSD([sQuery(id+"F0.wireOp",EDGE,"E25.0"),sQuery(id+"F0.wireOp",EDGE,"E25.1"),sQuery(id+"F0.wireOp",EDGE,"E25.2"),sQuery(id+"F0.wireOp",EDGE,"E25.3"),sQuery(id+"F0.wireOp",EDGE,"E25.4"),sQuery(id+"F0.wireOp",EDGE,"E25.5"),sQuery(id+"F0.wireOp",EDGE,"E25.6"),sQuery(id+"F0.wireOp",EDGE,"E25.7")])],"isStart":false})})});
            extrude(context, id + "F13", {"entities" : qUnion([Q0]), "operationType" : NewBodyOperationType.REMOVE, "endBound" : BoundingType.UP_TO_SURFACE, "endBoundEntityFace" : qUnion([Q1]), "depth" : 25 * mm});
        }
        {
            var Q0;
            Q0=makeQuery(id+"F3.boolean.opBoolean","COPY",EDGE,{"derivedFrom":makeQuery(id+"F3.opExtrude","CAP_EDGE",EDGE,{"disambiguationData":[OSD([sQuery(id+"F0.wireOp",EDGE,"E25.6")])],"isStart":false})});
            var Q1;
            Q1=makeQuery(id+"F8.boolean.opBoolean","INTERSECT",EDGE,{"derivedFrom":[makeQuery(id+"F5.opExtrude","SWEPT_FACE",FACE,{"disambiguationData":[OSD([sQuery(id+"F4.wireOp",EDGE,"E30")])]}),makeQuery(id+"F8.opExtrude","CAP_FACE",FACE,{"disambiguationData":[OSD([sQuery(id+"F7.wireOp",EDGE,"E67")])],"isStart":false})]});
            var Q2;
            Q2=makeQuery(id+"F8.boolean.opBoolean","INTERSECT",EDGE,{"disambiguationData":[OD(1.0)],"derivedFrom":[makeQuery(id+"F5.opExtrude","SWEPT_FACE",FACE,{"disambiguationData":[OSD([sQuery(id+"F4.wireOp",EDGE,"E30")])]}),makeQuery(id+"F8.opExtrude","SWEPT_FACE",FACE,{"disambiguationData":[OSD([sQuery(id+"F7.wireOp",EDGE,"E67")])]})]});
            var Q3;
            {var subQ0=sQuery(id+"F4.wireOp",EDGE,"E30");Q3=makeQuery(id+"F8.boolean.opBoolean","SPLIT",EDGE,{"disambiguationData":[TD([makeQuery(id+"F5.opExtrude","SWEPT_FACE",FACE,{"disambiguationData":[OSD([sQuery(id+"F4.wireOp",EDGE,"E35.filletArc")])]})])],"derivedFrom":makeQuery(id+"F5.opExtrude","CAP_EDGE",EDGE,{"disambiguationData":[OSD([subQ0])],"isStart":false})});}
            var Q4;
            {var subQ0=sQuery(id+"F0.wireOp",EDGE,"E25.7");var subQ1=sQuery(id+"F0.wireOp",EDGE,"E25.1");var subQ2=sQuery(id+"F0.wireOp",EDGE,"E25.6");var subQ3=sQuery(id+"F0.wireOp",EDGE,"E25.5");var subQ4=sQuery(id+"F0.wireOp",EDGE,"E25.4");var subQ5=sQuery(id+"F0.wireOp",EDGE,"E25.0");var subQ6=sQuery(id+"F0.wireOp",EDGE,"E25.2");var subQ7=sQuery(id+"F0.wireOp",EDGE,"E25.3");Q4=makeQuery(id+"F8.boolean.opBoolean","INTERSECT",EDGE,{"derivedFrom":[makeQuery(id+"F5.boolean.opBoolean","SPLIT",FACE,{"disambiguationData":[TD([makeQuery(id+"F2.opExtrude","SWEPT_FACE",FACE,{"disambiguationData":[OSD([subQ5])]})])],"derivedFrom":makeQuery(id+"F3.boolean.opBoolean","COPY",FACE,{"derivedFrom":makeQuery(id+"F3.opExtrude","CAP_FACE",FACE,{"disambiguationData":[OSD([subQ5,subQ1,subQ6,subQ7,subQ4,subQ3,subQ2,subQ0])],"isStart":false})})}),makeQuery(id+"F8.opExtrude","SWEPT_FACE",FACE,{"disambiguationData":[OSD([sQuery(id+"F7.wireOp",EDGE,"E67")])]})]});}
            var Q5;
            Q5=makeQuery(id+"F8.boolean.opBoolean","INTERSECT",EDGE,{"disambiguationData":[OD(0.0)],"derivedFrom":[makeQuery(id+"F5.opExtrude","SWEPT_FACE",FACE,{"disambiguationData":[OSD([sQuery(id+"F4.wireOp",EDGE,"E30")])]}),makeQuery(id+"F8.opExtrude","SWEPT_FACE",FACE,{"disambiguationData":[OSD([sQuery(id+"F7.wireOp",EDGE,"E67")])]})]});
            fillet(context, id + "F14", {"entities" : qUnion([Q0, Q1, Q2, Q3, Q4, Q5]), "radius" : 3 * mm, "tangentPropagation" : true, "allowEdgeOverflow" : false});
        }
        {
            var Q0;
            Q0=makeQuery(id+"F1.opExtrude","CAP_EDGE",EDGE,{"disambiguationData":[OSD([sQuery(id+"F0.wireOp",EDGE,"E1.bottom")])],"isStart":false});
            fillet(context, id + "F15", {"entities" : qUnion([Q0]), "radius" : 2 * mm, "tangentPropagation" : true, "allowEdgeOverflow" : false});
        }
        {
            var Q0;
            {var subQ0=sQuery(id+"F0.wireOp",EDGE,"E22.filletArc");var subQ1=sQuery(id+"F0.wireOp",EDGE,"E7");var subQ2=sQuery(id+"F0.wireOp",EDGE,"E6");var subQ3=sQuery(id+"F0.wireOp",EDGE,"E5");var subQ4=sQuery(id+"F0.wireOp",EDGE,"E4");var subQ5=sQuery(id+"F0.wireOp",EDGE,"E1.bottom");var subQ6=sQuery(id+"F0.wireOp",EDGE,"E21.filletArc");var subQ7=sQuery(id+"F0.wireOp",EDGE,"E1.top");var subQ8=sQuery(id+"F0.wireOp",EDGE,"E1.left");var subQ9=sQuery(id+"F0.wireOp",EDGE,"E1.right");var subQ10=sQuery(id+"F0.wireOp",EDGE,"E23.filletArc");var subQ11=sQuery(id+"F0.wireOp",EDGE,"E24.filletArc");Q0=makeQuery(id+"F2.boolean.opBoolean","SPLIT",FACE,{"disambiguationData":[TD([makeQuery(id+"F1.opExtrude","SWEPT_FACE",FACE,{"disambiguationData":[OSD([subQ5])]})])],"derivedFrom":makeQuery(id+"F1.opExtrude","CAP_FACE",FACE,{"disambiguationData":[OSD([subQ5,subQ7,subQ8,subQ9,subQ4,subQ3,subQ2,subQ1,subQ6,subQ0,subQ10,subQ11])],"isStart":true})});}
            var sketch = newSketch(context, id + "F16", { "sketchPlane" : qUnion([Q0])});
            skLineSegment(sketch, "E79", {"start": v(0, 90) * mm, "end": v(0, 120) * mm, "construction": true});
            skCircle(sketch, "E80", {"center": v(0, 120) * mm, "radius": 6 * mm});
            skLineSegment(sketch, "E81", {"start": v(-33, 90) * mm, "end": v(-15, 108) * mm});
            skLineSegment(sketch, "E82", {"start": v(-15, 108) * mm, "end": v(-15, 120) * mm});
            skLineSegment(sketch, "E83", {"start": v(14.97, 107.06) * mm, "end": v(32.04, 90) * mm});
            skLineSegment(sketch, "E84", {"start": v(14.97, 107.06) * mm, "end": v(14.97, 119.06) * mm});
            skArc(sketch, "E85", {"start": v(14.97, 119.06) * mm, "mid": v(0.47, 135) * mm, "end": v(-15, 120) * mm});
            skLineSegment(sketch, "E86", {"start": v(-80, 0) * mm, "end": v(80, 0) * mm, "construction": true});
            skLineSegment(sketch, "E87.MirrorCS", {"start": v(14.97, -107.06) * mm, "end": v(14.97, -119.06) * mm});
            skLineSegment(sketch, "E88.MirrorCS", {"start": v(-15, -108) * mm, "end": v(-15, -120) * mm});
            skCircle(sketch, "E89.MirrorC", {"center": v(0, -120) * mm, "radius": 6 * mm});
            skArc(sketch, "E90.MirrorCS", {"start": v(14.97, -119.06) * mm, "mid": v(0.47, -135) * mm, "end": v(-15, -120) * mm});
            skLineSegment(sketch, "E91.MirrorCS", {"start": v(0, -90) * mm, "end": v(0, -120) * mm, "construction": true});
            skLineSegment(sketch, "E92.MirrorCS", {"start": v(14.97, -107.06) * mm, "end": v(32.04, -90) * mm});
            skLineSegment(sketch, "E93.MirrorCS", {"start": v(-33, -90) * mm, "end": v(-15, -108) * mm});
            skSolve(sketch);
        }
        {
            var Q0;
            {var subQ1=sQuery(id+"F16.wireOp",EDGE,"E81");Q0=makeQuery(id+"F16.imprint","IMPRINT",FACE,{"disambiguationData":[TD([[makeQuery(id+"F16.imprint","IMPRINT",EDGE,{"derivedFrom":subQ1}),-1.0]])]});}
            var Q1;
            Q1=makeQuery(id+"F16.imprint","IMPRINT",FACE,{"disambiguationData":[TD([[makeQuery(id+"F16.imprint","IMPRINT",EDGE,{"derivedFrom":makeQuery(id+"F1.opExtrude","CAP_EDGE",EDGE,{"disambiguationData":[OSD([sQuery(id+"F0.wireOp",EDGE,"E1.left")])],"isStart":true})}),-1.0]])]});
            var Q2;
            Q2=makeQuery(id+"F16.imprint","IMPRINT",FACE,{"disambiguationData":[TD([[makeQuery(id+"F16.imprint","IMPRINT",EDGE,{"derivedFrom":sQuery(id+"F16.wireOp",EDGE,"E87.MirrorCS")}),-1.0]])]});
            var Q3;
            Q3=makeQuery(id+"F2.opExtrude","CAP_FACE",FACE,{"disambiguationData":[OSD([sQuery(id+"F0.wireOp",EDGE,"E12"),sQuery(id+"F0.wireOp",EDGE,"E13"),sQuery(id+"F0.wireOp",EDGE,"E14"),sQuery(id+"F0.wireOp",EDGE,"E15"),sQuery(id+"F0.wireOp",EDGE,"E17.filletArc"),sQuery(id+"F0.wireOp",EDGE,"E18.filletArc"),sQuery(id+"F0.wireOp",EDGE,"E19.filletArc"),sQuery(id+"F0.wireOp",EDGE,"E20.filletArc"),sQuery(id+"F0.wireOp",EDGE,"E25.0"),sQuery(id+"F0.wireOp",EDGE,"E25.1"),sQuery(id+"F0.wireOp",EDGE,"E25.2"),sQuery(id+"F0.wireOp",EDGE,"E25.3"),sQuery(id+"F0.wireOp",EDGE,"E25.4"),sQuery(id+"F0.wireOp",EDGE,"E25.5"),sQuery(id+"F0.wireOp",EDGE,"E25.6"),sQuery(id+"F0.wireOp",EDGE,"E25.7")])],"isStart":false});
            extrude(context, id + "F17", {"entities" : qUnion([Q0, Q1, Q2]), "operationType" : NewBodyOperationType.ADD, "endBound" : BoundingType.UP_TO_SURFACE, "endBoundEntityFace" : qUnion([Q3]), "depth" : 25 * mm});
        }
    });
